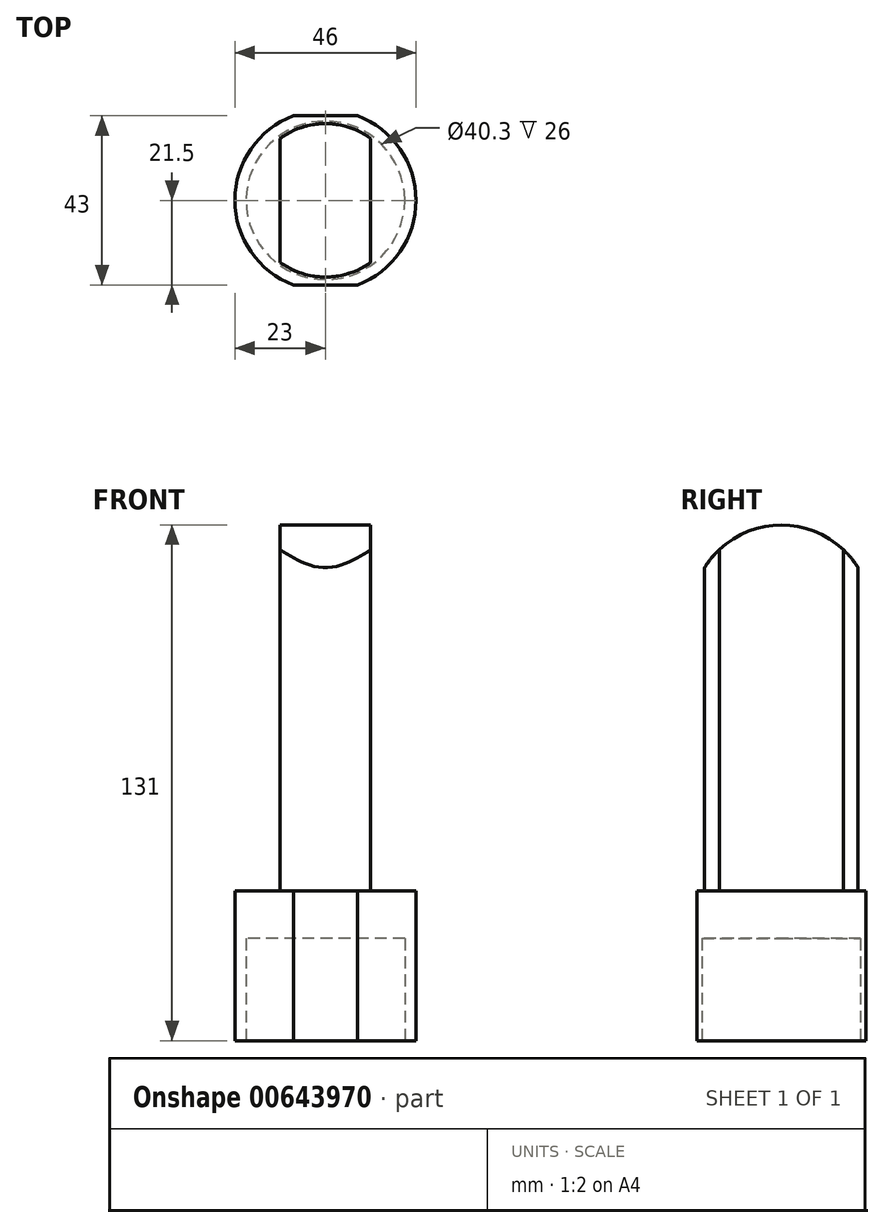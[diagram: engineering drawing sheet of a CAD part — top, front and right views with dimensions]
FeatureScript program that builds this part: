
annotation { "Feature Type Name" : "Feature", "Feature Type Description" : "" }
export const myFeature = defineFeature(function(context is Context, id is Id, definition is map)
    precondition{}
    {
        {
            var Q0;
            Q0=qCreatedBy(makeId("Top.planeOp"),FACE);
            var sketch = newSketch(context, id + "F0", { "sketchPlane" : qUnion([Q0])});
            skArc(sketch, "E0", {"start": v(-8.17, 21.5) * mm, "mid": v(-23, 0) * mm, "end": v(-8.17, -21.5) * mm});
            skLineSegment(sketch, "E1", {"start": v(-8.17, 21.5) * mm, "end": v(8.17, 21.5) * mm});
            skLineSegment(sketch, "E2.MirrorCS", {"start": v(-8.17, -21.5) * mm, "end": v(8.17, -21.5) * mm});
            skArc(sketch, "E3.trimOffspring", {"start": v(8.17, -21.5) * mm, "mid": v(23, 0) * mm, "end": v(8.17, 21.5) * mm});
            skSolve(sketch);
        }
        {
            var Q0;
            Q0 = qSketchRegion(id + "F0", true);
            extrude(context, id + "F1", {"entities" : qUnion([Q0]), "depth" : 38 * mm, "offsetDistance" : 25 * mm});
        }
        {
            var Q0;
            Q0=qCreatedBy(makeId("Top.planeOp"),FACE);
            var sketch = newSketch(context, id + "F2", { "sketchPlane" : qUnion([Q0])});
            skCircle(sketch, "E4", {"center": v(0, 0) * mm, "radius": 20.15 * mm});
            skSolve(sketch);
        }
        {
            var Q0;
            Q0 = qSketchRegion(id + "F2", true);
            extrude(context, id + "F3", {"entities" : qUnion([Q0]), "operationType" : NewBodyOperationType.REMOVE, "depth" : 26 * mm, "offsetDistance" : 25 * mm});
        }
        {
            var Q0;
            Q0=makeQuery(id+"F1.opExtrude","CAP_FACE",FACE,{"disambiguationData":[OSD([sQuery(id+"F0.wireOp",EDGE,"E0"),sQuery(id+"F0.wireOp",EDGE,"E1"),sQuery(id+"F0.wireOp",EDGE,"E2.MirrorCS"),sQuery(id+"F0.wireOp",EDGE,"E3.trimOffspring")])],"isStart":false});
            var sketch = newSketch(context, id + "F4", { "sketchPlane" : qUnion([Q0])});
            skArc(sketch, "E5", {"start": v(-11.5, -15.75) * mm, "mid": v(0, -19.5) * mm, "end": v(11.5, -15.75) * mm});
            skLineSegment(sketch, "E6", {"start": v(-11.5, 15.75) * mm, "end": v(-11.5, -15.75) * mm});
            skLineSegment(sketch, "E7.MirrorCS", {"start": v(11.5, 15.75) * mm, "end": v(11.5, -15.75) * mm});
            skArc(sketch, "E8.trimOffspring", {"start": v(11.5, 15.75) * mm, "mid": v(0, 19.5) * mm, "end": v(-11.5, 15.75) * mm});
            skSolve(sketch);
        }
        {
            var Q0;
            Q0 = qSketchRegion(id + "F4", true);
            extrude(context, id + "F5", {"entities" : qUnion([Q0]), "operationType" : NewBodyOperationType.ADD, "depth" : 93 * mm, "offsetDistance" : 25 * mm});
        }
        {
            var Q0;
            Q0=qCreatedBy(makeId("Right.planeOp"),FACE);
            var sketch = newSketch(context, id + "F6", { "sketchPlane" : qUnion([Q0])});
            skArc(sketch, "E9", {"start": v(22.72, 111.59) * mm, "mid": v(-1.7, 130.94) * mm, "end": v(-23, 108.2) * mm});
            skLineSegment(sketch, "E10", {"start": v(-23, 108.2) * mm, "end": v(-40.64, 148.26) * mm});
            skLineSegment(sketch, "E11", {"start": v(-40.64, 148.26) * mm, "end": v(37.95, 148.26) * mm});
            skLineSegment(sketch, "E12", {"start": v(37.95, 148.26) * mm, "end": v(22.72, 111.59) * mm});
            skSolve(sketch);
        }
        {
            var Q0;
            Q0 = qSketchRegion(id + "F6", true);
            extrude(context, id + "F7", {"entities" : qUnion([Q0]), "operationType" : NewBodyOperationType.REMOVE, "endBound" : BoundingType.SYMMETRIC, "oppositeDirection" : true, "depth" : 25 * mm, "offsetDistance" : 25 * mm});
        }
    });
